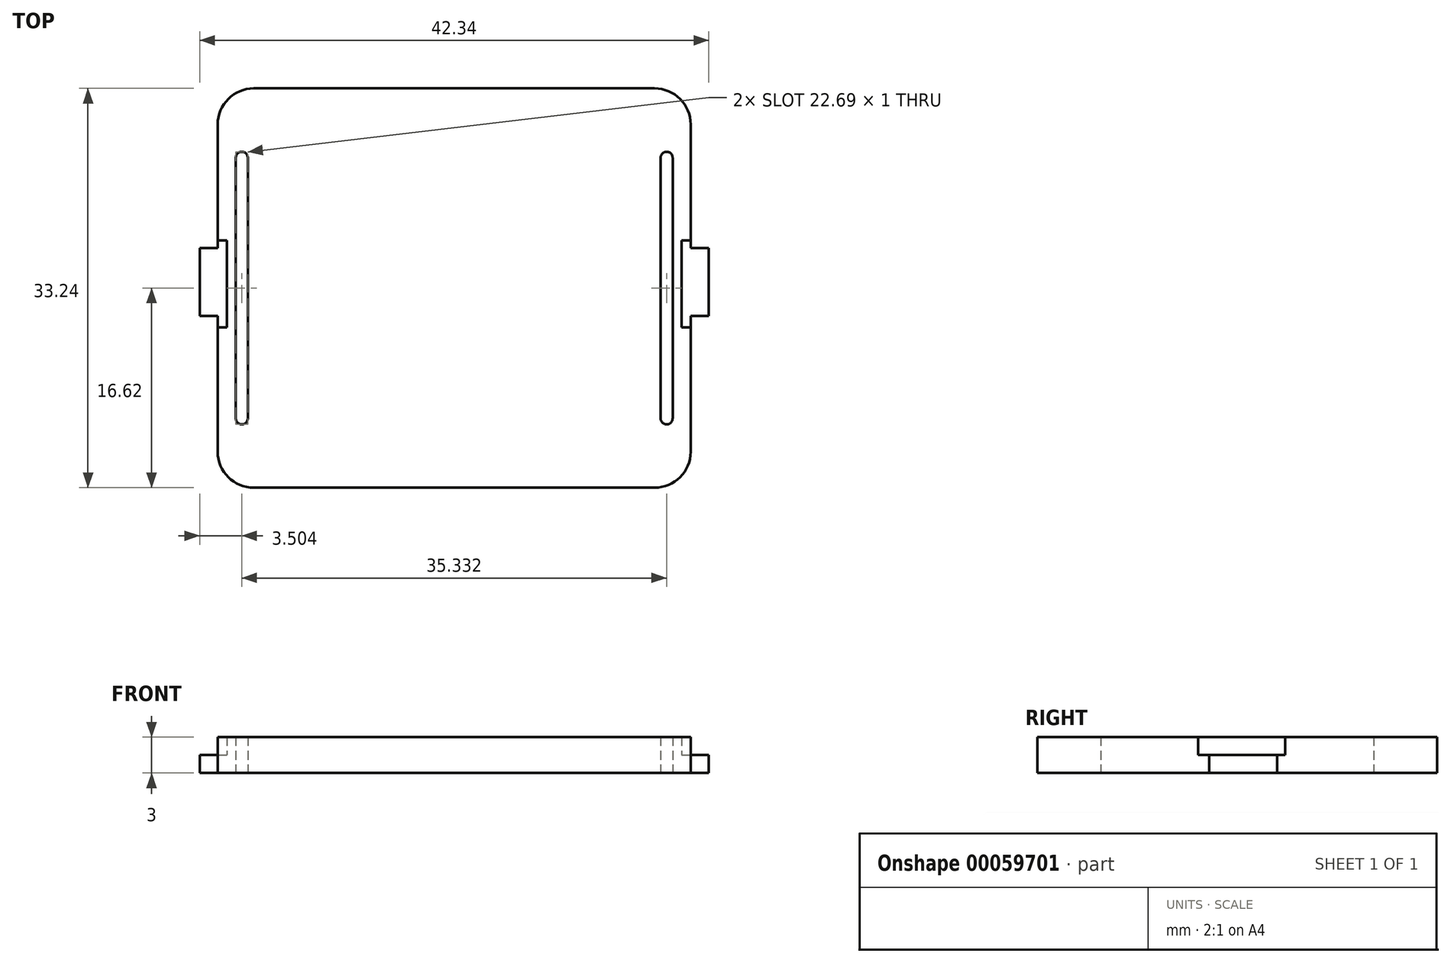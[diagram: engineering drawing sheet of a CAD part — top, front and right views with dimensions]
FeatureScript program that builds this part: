
annotation { "Feature Type Name" : "Feature", "Feature Type Description" : "" }
export const myFeature = defineFeature(function(context is Context, id is Id, definition is map)
    precondition{}
    {
        {
            assignVariable(context, id + "F0", {"name" : "LidT", "anyValue" : 3});
        }
        {
            var Q0;
            Q0=qCreatedBy(makeId("Top.planeOp"),FACE);
            var sketch = newSketch(context, id + "F1", { "sketchPlane" : qUnion([Q0])});
            skLineSegment(sketch, "E0.bottom", {"start": v(-16.67, 16.62) * mm, "end": v(16.67, 16.62) * mm});
            skLineSegment(sketch, "E0.top", {"start": v(-16.67, -16.62) * mm, "end": v(16.67, -16.62) * mm});
            skLineSegment(sketch, "E0.left", {"start": v(-19.67, 13.62) * mm, "end": v(-19.67, -13.62) * mm});
            skLineSegment(sketch, "E0.right", {"start": v(19.67, 13.62) * mm, "end": v(19.67, -13.62) * mm});
            skPoint(sketch, "E1.visualSharp", {"position": v(-19.67, 16.62) * mm});
            skArc(sketch, "E1.filletArc", {"start": v(-16.67, 16.62) * mm, "mid": v(-18.79, 15.74) * mm, "end": v(-19.67, 13.62) * mm});
            skPoint(sketch, "E2.visualSharp", {"position": v(19.67, 16.62) * mm});
            skArc(sketch, "E2.filletArc", {"start": v(19.67, 13.62) * mm, "mid": v(18.79, 15.74) * mm, "end": v(16.67, 16.62) * mm});
            skPoint(sketch, "E3.visualSharp", {"position": v(19.67, -16.62) * mm});
            skArc(sketch, "E3.filletArc", {"start": v(16.67, -16.62) * mm, "mid": v(18.79, -15.74) * mm, "end": v(19.67, -13.62) * mm});
            skPoint(sketch, "E4.visualSharp", {"position": v(-19.67, -16.62) * mm});
            skArc(sketch, "E4.filletArc", {"start": v(-19.67, -13.62) * mm, "mid": v(-18.79, -15.74) * mm, "end": v(-16.67, -16.62) * mm});
            skLineSegment(sketch, "E5", {"start": v(-17.67, 10.85) * mm, "end": v(-17.67, -10.85) * mm});
            skLineSegment(sketch, "E6", {"start": v(-19.67, 3.98) * mm, "end": v(-18.92, 3.98) * mm});
            skLineSegment(sketch, "E7", {"start": v(-18.92, 3.98) * mm, "end": v(-18.92, -3.27) * mm});
            skLineSegment(sketch, "E8", {"start": v(-18.92, -3.27) * mm, "end": v(-19.67, -3.27) * mm});
            skLineSegment(sketch, "E9", {"start": v(-19.67, 3.33) * mm, "end": v(-21.17, 3.33) * mm});
            skLineSegment(sketch, "E10", {"start": v(-21.17, 3.33) * mm, "end": v(-21.17, -2.33) * mm});
            skLineSegment(sketch, "E11", {"start": v(-21.17, -2.33) * mm, "end": v(-19.67, -2.33) * mm});
            skArc(sketch, "E12.0.startCap", {"start": v(-18.17, 10.85) * mm, "mid": v(-17.67, 11.35) * mm, "end": v(-17.17, 10.85) * mm});
            skArc(sketch, "E12.0.endCap", {"start": v(-17.17, -10.85) * mm, "mid": v(-17.67, -11.35) * mm, "end": v(-18.17, -10.85) * mm});
            skLineSegment(sketch, "E12.0.left", {"start": v(-17.17, 10.85) * mm, "end": v(-17.17, -10.85) * mm});
            skLineSegment(sketch, "E12.0.right", {"start": v(-18.17, 10.85) * mm, "end": v(-18.17, -10.85) * mm});
            skArc(sketch, "E13.MirrorCS", {"start": v(18.17, 10.85) * mm, "mid": v(17.67, 11.35) * mm, "end": v(17.17, 10.85) * mm});
            skArc(sketch, "E14.MirrorCS", {"start": v(17.17, -10.85) * mm, "mid": v(17.67, -11.35) * mm, "end": v(18.17, -10.85) * mm});
            skLineSegment(sketch, "E15.MirrorCS", {"start": v(19.67, 3.98) * mm, "end": v(18.92, 3.98) * mm});
            skLineSegment(sketch, "E16.MirrorCS", {"start": v(18.92, -3.27) * mm, "end": v(19.67, -3.27) * mm});
            skLineSegment(sketch, "E17.MirrorCS", {"start": v(21.17, 3.33) * mm, "end": v(21.17, -2.33) * mm});
            skLineSegment(sketch, "E18.MirrorCS", {"start": v(17.17, 10.85) * mm, "end": v(17.17, -10.85) * mm});
            skLineSegment(sketch, "E19.MirrorCS", {"start": v(21.17, -2.33) * mm, "end": v(19.67, -2.33) * mm});
            skLineSegment(sketch, "E20.MirrorCS", {"start": v(17.67, 10.85) * mm, "end": v(17.67, -10.85) * mm});
            skLineSegment(sketch, "E21.MirrorCS", {"start": v(18.92, 3.98) * mm, "end": v(18.92, -3.27) * mm});
            skLineSegment(sketch, "E22.MirrorCS", {"start": v(18.17, 10.85) * mm, "end": v(18.17, -10.85) * mm});
            skLineSegment(sketch, "E23.MirrorCS", {"start": v(19.67, 3.33) * mm, "end": v(21.17, 3.33) * mm});
            skSolve(sketch);
        }
        {
            var Q0;
            Q0=makeQuery(id+"F1.imprint","IMPRINT",FACE,{"disambiguationData":[TD([[makeQuery(id+"F1.imprint","IMPRINT",EDGE,{"derivedFrom":sQuery(id+"F1.wireOp",EDGE,"E0.bottom")}),-1.0]])]});
            extrude(context, id + "F2", {"entities" : qUnion([Q0]), "depth" : (getVariable(context, 'LidT')) * mm});
        }
        {
            var Q0;
            {var subQ0=sQuery(id+"F1.wireOp",EDGE,"E9");Q0=makeQuery(id+"F1.imprint","IMPRINT",FACE,{"disambiguationData":[TD([[makeQuery(id+"F1.imprint","IMPRINT",EDGE,{"derivedFrom":subQ0}),1.0]])]});}
            var Q1;
            {var subQ3=sQuery(id+"F1.wireOp",EDGE,"E6");Q1=makeQuery(id+"F1.imprint","IMPRINT",FACE,{"disambiguationData":[TD([[makeQuery(id+"F1.imprint","IMPRINT",EDGE,{"derivedFrom":subQ3}),-1.0]])]});}
            var Q2;
            {var subQ0=sQuery(id+"F1.wireOp",EDGE,"E15.MirrorCS");Q2=makeQuery(id+"F1.imprint","IMPRINT",FACE,{"disambiguationData":[TD([[makeQuery(id+"F1.imprint","IMPRINT",EDGE,{"derivedFrom":subQ0}),1.0]])]});}
            var Q3;
            Q3=makeQuery(id+"F1.imprint","IMPRINT",FACE,{"disambiguationData":[TD([[makeQuery(id+"F1.imprint","IMPRINT",EDGE,{"derivedFrom":sQuery(id+"F1.wireOp",EDGE,"E17.MirrorCS")}),-1.0]])]});
            extrude(context, id + "F3", {"entities" : qUnion([Q0, Q1, Q2, Q3]), "operationType" : NewBodyOperationType.ADD, "depth" : (getVariable(context, 'LidT') / 2) * mm});
        }
    });
